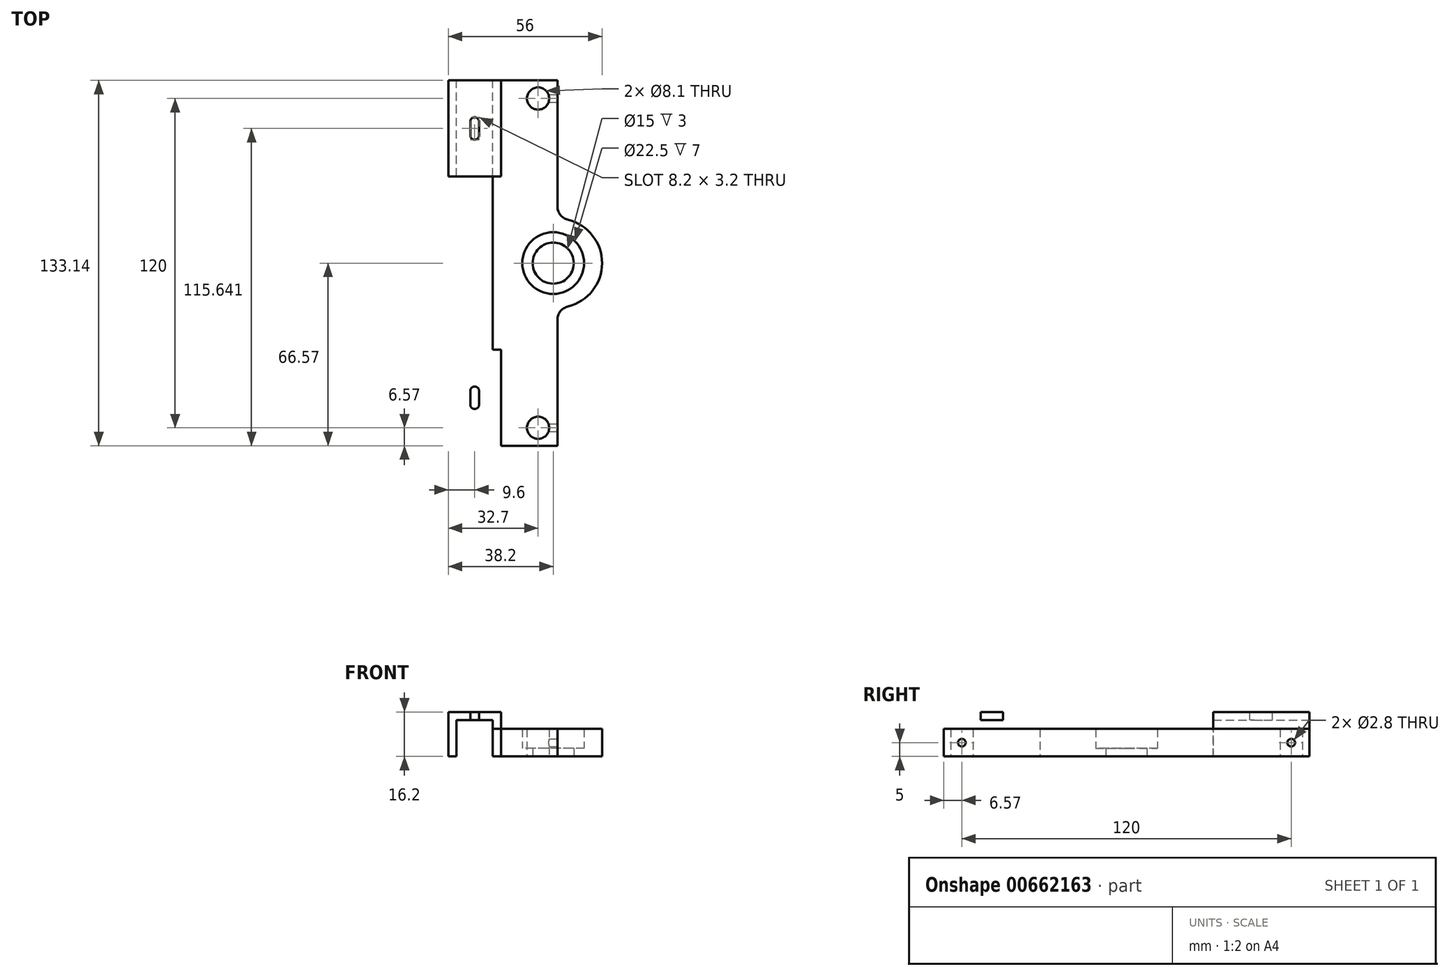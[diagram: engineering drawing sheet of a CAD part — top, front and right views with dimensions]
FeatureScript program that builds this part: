
annotation { "Feature Type Name" : "Feature", "Feature Type Description" : "" }
export const myFeature = defineFeature(function(context is Context, id is Id, definition is map)
    precondition{}
    {
        {
            var Q0;
            Q0=qCreatedBy(makeId("Top.planeOp"),FACE);
            var sketch = newSketch(context, id + "F0", { "sketchPlane" : qUnion([Q0])});
            skCircle(sketch, "E0", {"center": v(0, 0) * mm, "radius": 7.5 * mm});
            skLineSegment(sketch, "E1.rect.bottom", {"start": v(-22, -66.57) * mm, "end": v(22, -66.57) * mm});
            skLineSegment(sketch, "E1.rect.top", {"start": v(-22, 66.57) * mm, "end": v(22, 66.57) * mm});
            skLineSegment(sketch, "E1.rect.left", {"start": v(-22, -66.57) * mm, "end": v(-22, 66.57) * mm});
            skLineSegment(sketch, "E1.rect.right", {"start": v(22, -66.57) * mm, "end": v(22, 66.57) * mm});
            skCircle(sketch, "E2", {"center": v(0, 0) * mm, "radius": 11.25 * mm});
            skCircle(sketch, "E3", {"center": v(-5.5, -60) * mm, "radius": 4.05 * mm});
            skCircle(sketch, "E4", {"center": v(-5.5, 60) * mm, "radius": 4.05 * mm});
            skSolve(sketch);
        }
        {
            var Q0;
            Q0=makeQuery(id+"F0.imprint","IMPRINT",FACE,{"disambiguationData":[TD([[makeQuery(id+"F0.imprint","IMPRINT",EDGE,{"derivedFrom":sQuery(id+"F0.wireOp",EDGE,"E0")}),-1.0]])]});
            extrude(context, id + "F1", {"entities" : qUnion([Q0]), "depth" : 3 * mm});
        }
        {
            var Q0;
            Q0=makeQuery(id+"F0.imprint","IMPRINT",FACE,{"disambiguationData":[TD([[makeQuery(id+"F0.imprint","IMPRINT",EDGE,{"derivedFrom":sQuery(id+"F0.wireOp",EDGE,"E1.rect.bottom")}),1.0]])]});
            extrude(context, id + "F2", {"entities" : qUnion([Q0]), "operationType" : NewBodyOperationType.ADD, "depth" : 10 * mm});
        }
        {
            var Q0;
            Q0=makeQuery(id+"F2.opExtrude","CAP_FACE",FACE,{"disambiguationData":[OSD([sQuery(id+"F0.wireOp",EDGE,"E1.rect.bottom"),sQuery(id+"F0.wireOp",EDGE,"E1.rect.top"),sQuery(id+"F0.wireOp",EDGE,"E1.rect.left"),sQuery(id+"F0.wireOp",EDGE,"E1.rect.right"),sQuery(id+"F0.wireOp",EDGE,"E2"),sQuery(id+"F0.wireOp",EDGE,"E3"),sQuery(id+"F0.wireOp",EDGE,"E4")])],"isStart":false});
            var sketch = newSketch(context, id + "F3", { "sketchPlane" : qUnion([Q0])});
            skLineSegment(sketch, "E5", {"start": v(1.55, -66.57) * mm, "end": v(1.55, -16.25) * mm});
            skLineSegment(sketch, "E6", {"start": v(1.55, -16.25) * mm, "end": v(22, -16.25) * mm});
            skLineSegment(sketch, "E7", {"start": v(1.55, 66.57) * mm, "end": v(1.55, 16.25) * mm});
            skLineSegment(sketch, "E8", {"start": v(1.55, 16.25) * mm, "end": v(22, 16.25) * mm});
            skSolve(sketch);
        }
        {
            var Q0;
            {var subQ4=sQuery(id+"F3.wireOp",EDGE,"E5");Q0=makeQuery(id+"F3.imprint","IMPRINT",FACE,{"disambiguationData":[TD([[makeQuery(id+"F3.imprint","IMPRINT",EDGE,{"derivedFrom":subQ4}),-1.0]])]});}
            var Q1;
            {var subQ4=sQuery(id+"F3.wireOp",EDGE,"E7");Q1=makeQuery(id+"F3.imprint","IMPRINT",FACE,{"disambiguationData":[TD([[makeQuery(id+"F3.imprint","IMPRINT",EDGE,{"derivedFrom":subQ4}),1.0]])]});}
            extrude(context, id + "F4", {"entities" : qUnion([Q0, Q1]), "operationType" : NewBodyOperationType.REMOVE, "endBound" : BoundingType.UP_TO_NEXT, "oppositeDirection" : true, "depth" : 25 * mm});
        }
        {
            var Q0;
            Q0=makeQuery(id+"F2.opExtrude","CAP_FACE",FACE,{"disambiguationData":[OSD([sQuery(id+"F0.wireOp",EDGE,"E1.rect.bottom"),sQuery(id+"F0.wireOp",EDGE,"E1.rect.top"),sQuery(id+"F0.wireOp",EDGE,"E1.rect.left"),sQuery(id+"F0.wireOp",EDGE,"E1.rect.right"),sQuery(id+"F0.wireOp",EDGE,"E2"),sQuery(id+"F0.wireOp",EDGE,"E3"),sQuery(id+"F0.wireOp",EDGE,"E4")])],"isStart":false});
            var sketch = newSketch(context, id + "F5", { "sketchPlane" : qUnion([Q0])});
            skArc(sketch, "E9", {"start": v(1.55, -16.25) * mm, "mid": v(17.8, 0) * mm, "end": v(1.55, 16.25) * mm});
            skSolve(sketch);
        }
        {
            var Q0;
            Q0=makeQuery(id+"F5.imprint","IMPRINT",FACE,{"disambiguationData":[TD([[makeQuery(id+"F5.imprint","IMPRINT",EDGE,{"derivedFrom":sQuery(id+"F5.wireOp",EDGE,"E9")}),-1.0]])]});
            extrude(context, id + "F6", {"entities" : qUnion([Q0]), "operationType" : NewBodyOperationType.REMOVE, "endBound" : BoundingType.UP_TO_NEXT, "oppositeDirection" : true, "depth" : 25 * mm});
        }
        {
            var Q0;
            Q0=makeQuery(id+"F2.opExtrude","SWEPT_FACE",FACE,{"disambiguationData":[OSD([sQuery(id+"F0.wireOp",EDGE,"E1.rect.bottom")])]});
            var sketch = newSketch(context, id + "F7", { "sketchPlane" : qUnion([Q0])});
            skLineSegment(sketch, "E10", {"start": v(-22, 0) * mm, "end": v(-22, 0) * mm});
            skLineSegment(sketch, "E11", {"start": v(-22, 13.2) * mm, "end": v(-22, 0) * mm});
            skLineSegment(sketch, "E12", {"start": v(-22, 13.2) * mm, "end": v(-35.2, 13.2) * mm});
            skLineSegment(sketch, "E13", {"start": v(-35.2, 0) * mm, "end": v(-35.2, 13.2) * mm});
            skLineSegment(sketch, "E14", {"start": v(-35.2, 0) * mm, "end": v(-38.2, 0) * mm});
            skLineSegment(sketch, "E15", {"start": v(-38.2, 0) * mm, "end": v(-38.2, 16.2) * mm});
            skLineSegment(sketch, "E16", {"start": v(-22, 10) * mm, "end": v(-19, 10) * mm});
            skLineSegment(sketch, "E17", {"start": v(-19, 10) * mm, "end": v(-19, 16.2) * mm});
            skLineSegment(sketch, "E18", {"start": v(-19, 16.2) * mm, "end": v(-38.2, 16.2) * mm});
            skSolve(sketch);
        }
        {
            var Q0;
            Q0=qSketchRegion(id+"F7",true);
            var Q1;
            Q1=makeQuery(id+"F7.imprint","IMPRINT",FACE,{"disambiguationData":[TD([[makeQuery(id+"F7.imprint","IMPRINT",EDGE,{"derivedFrom":sQuery(id+"F7.wireOp",EDGE,"E10")}),-1.0]])]});
            var Q2;
            Q2=makeQuery(id+"F2.opExtrude","SWEPT_FACE",FACE,{"disambiguationData":[OSD([sQuery(id+"F0.wireOp",EDGE,"E1.rect.top")])]});
            extrude(context, id + "F8", {"entities" : qUnion([Q0, Q1]), "operationType" : NewBodyOperationType.ADD, "oppositeDirection" : true, "endBoundEntityFace" : qUnion([Q2]), "depth" : 35 * mm});
        }
        {
            var Q0;
            Q0=makeQuery(id+"F4.boolean.opBoolean","COPY",FACE,{"derivedFrom":makeQuery(id+"F4.opExtrude","SWEPT_FACE",FACE,{"disambiguationData":[OSD([sQuery(id+"F3.wireOp",EDGE,"E5")])]})});
            var sketch = newSketch(context, id + "F9", { "sketchPlane" : qUnion([Q0])});
            skCircle(sketch, "E19", {"center": v(-60, 5) * mm, "radius": 1.4 * mm});
            skPoint(sketch, "E19.centerSnap0", {"position": v(-66.57, 5) * mm});
            skCircle(sketch, "E20", {"center": v(60, 5) * mm, "radius": 1.4 * mm});
            skSolve(sketch);
        }
        {
            var Q0;
            Q0=makeQuery(id+"F9.imprint","IMPRINT",FACE,{"disambiguationData":[TD([[makeQuery(id+"F9.imprint","IMPRINT",EDGE,{"derivedFrom":sQuery(id+"F9.wireOp",EDGE,"E19")}),1.0]])]});
            var Q1;
            Q1=makeQuery(id+"F9.imprint","IMPRINT",FACE,{"disambiguationData":[TD([[makeQuery(id+"F9.imprint","IMPRINT",EDGE,{"derivedFrom":sQuery(id+"F9.wireOp",EDGE,"E20")}),1.0]])]});
            var Q2;
            Q2=makeQuery(id+"F1.opExtrude","SWEPT_BODY",BODY,{"disambiguationData":[OSD([sQuery(id+"F0.wireOp",EDGE,"E0"),sQuery(id+"F0.wireOp",EDGE,"E2")])]});
            extrude(context, id + "F10", {"entities" : qUnion([Q0, Q1]), "operationType" : NewBodyOperationType.REMOVE, "endBound" : BoundingType.UP_TO_BODY, "oppositeDirection" : true, "endBoundEntityBody" : qUnion([Q2]), "depth" : 25 * mm});
        }
        {
            var Q0;
            Q0=makeQuery(id+"F4.boolean.opBoolean","COPY",EDGE,{"derivedFrom":makeQuery(id+"F4.opExtrude","SWEPT_EDGE",EDGE,{"disambiguationData":[OSD([sQuery(id+"F0.wireOp",EDGE,"E1.rect.top"),sQuery(id+"F3.wireOp",EDGE,"E7")])]})});
            var Q1;
            Q1=makeQuery(id+"F4.boolean.opBoolean","COPY",EDGE,{"derivedFrom":makeQuery(id+"F4.opExtrude","SWEPT_EDGE",EDGE,{"disambiguationData":[OSD([sQuery(id+"F0.wireOp",EDGE,"E1.rect.bottom"),sQuery(id+"F3.wireOp",EDGE,"E5")])]})});
            var Q2;
            {var subQ0=sQuery(id+"F3.wireOp",EDGE,"E5");var subQ1=sQuery(id+"F3.wireOp",EDGE,"E6");Q2=makeQuery(id+"F6.boolean.opBoolean","MERGE",EDGE,{"derivedFrom":[makeQuery(id+"F4.boolean.opBoolean","COPY",EDGE,{"derivedFrom":makeQuery(id+"F4.opExtrude","SWEPT_EDGE",EDGE,{"disambiguationData":[OSD([subQ0,subQ1])]})}),makeQuery(id+"F6.opExtrude","SWEPT_EDGE",EDGE,{"disambiguationData":[OSD([subQ0,subQ1,sQuery(id+"F5.wireOp",EDGE,"E9")])]})]});}
            var Q3;
            {var subQ0=sQuery(id+"F3.wireOp",EDGE,"E7");var subQ1=sQuery(id+"F3.wireOp",EDGE,"E8");Q3=makeQuery(id+"F6.boolean.opBoolean","MERGE",EDGE,{"derivedFrom":[makeQuery(id+"F4.boolean.opBoolean","COPY",EDGE,{"derivedFrom":makeQuery(id+"F4.opExtrude","SWEPT_EDGE",EDGE,{"disambiguationData":[OSD([subQ0,subQ1])]})}),makeQuery(id+"F6.opExtrude","SWEPT_EDGE",EDGE,{"disambiguationData":[OSD([sQuery(id+"F0.wireOp",EDGE,"E0"),sQuery(id+"F0.wireOp",EDGE,"E1.rect.bottom"),sQuery(id+"F0.wireOp",EDGE,"E1.rect.top"),sQuery(id+"F0.wireOp",EDGE,"E1.rect.left"),sQuery(id+"F0.wireOp",EDGE,"E1.rect.right"),sQuery(id+"F0.wireOp",EDGE,"E2"),sQuery(id+"F0.wireOp",EDGE,"E3"),sQuery(id+"F0.wireOp",EDGE,"E4"),subQ0,subQ1])]})]});}
            fillet(context, id + "F11", {"entities" : qUnion([Q0, Q1, Q2, Q3]), "radius" : 5 * mm, "tangentPropagation" : true, "allowEdgeOverflow" : false});
        }
        {
            var Q0;
            Q0=makeQuery(id+"F2.opExtrude","SWEPT_FACE",FACE,{"disambiguationData":[OSD([sQuery(id+"F0.wireOp",EDGE,"E1.rect.top")])]});
            var sketch = newSketch(context, id + "F12", { "sketchPlane" : qUnion([Q0])});
            skLineSegment(sketch, "E21.0.3", {"start": v(19, 10) * mm, "end": v(19, 16.2) * mm});
            skLineSegment(sketch, "E21.0.4", {"start": v(19, 16.2) * mm, "end": v(38.2, 16.2) * mm});
            skLineSegment(sketch, "E21.0.5", {"start": v(38.2, 16.2) * mm, "end": v(38.2, 0) * mm});
            skLineSegment(sketch, "E21.0.6", {"start": v(38.2, 0) * mm, "end": v(35.2, 0) * mm});
            skLineSegment(sketch, "E21.0.7", {"start": v(35.2, 0) * mm, "end": v(35.2, 13.2) * mm});
            skLineSegment(sketch, "E21.0.8", {"start": v(35.2, 13.2) * mm, "end": v(22, 13.2) * mm});
            skLineSegment(sketch, "E22", {"start": v(19, 10) * mm, "end": v(22, 10) * mm});
            skLineSegment(sketch, "E23", {"start": v(22, 10) * mm, "end": v(22, 13.2) * mm});
            skSolve(sketch);
        }
        {
            var Q0;
            Q0=qSketchRegion(id+"F12",true);
            var Q1;
            {var subQ1=sQuery(id+"F12.wireOp",EDGE,"E21.0.3");Q1=makeQuery(id+"F12.imprint","IMPRINT",FACE,{"disambiguationData":[TD([[makeQuery(id+"F12.imprint","IMPRINT",EDGE,{"derivedFrom":subQ1}),-1.0]])]});}
            extrude(context, id + "F13", {"entities" : qUnion([Q0, Q1]), "operationType" : NewBodyOperationType.ADD, "oppositeDirection" : true, "depth" : 35 * mm});
        }
        {
            var Q0;
            Q0=makeQuery(id+"F8.opExtrude","SWEPT_FACE",FACE,{"disambiguationData":[OSD([sQuery(id+"F7.wireOp",EDGE,"E18")])]});
            var sketch = newSketch(context, id + "F14", { "sketchPlane" : qUnion([Q0])});
            skArc(sketch, "E24.0.startCap", {"start": v(-30.2, -46.57) * mm, "mid": v(-28.6, -44.97) * mm, "end": v(-27, -46.57) * mm});
            skArc(sketch, "E24.0.endCap", {"start": v(-27, -51.57) * mm, "mid": v(-28.6, -53.17) * mm, "end": v(-30.2, -51.57) * mm});
            skLineSegment(sketch, "E24.0.left", {"start": v(-27, -46.57) * mm, "end": v(-27, -51.57) * mm});
            skLineSegment(sketch, "E24.0.right", {"start": v(-30.2, -46.57) * mm, "end": v(-30.2, -51.57) * mm});
            skArc(sketch, "E25.MirrorCS", {"start": v(-30.2, 46.57) * mm, "mid": v(-28.6, 44.97) * mm, "end": v(-27, 46.57) * mm});
            skLineSegment(sketch, "E26.MirrorCS", {"start": v(-27, 46.57) * mm, "end": v(-27, 51.57) * mm});
            skLineSegment(sketch, "E27.MirrorCS", {"start": v(-30.2, 46.57) * mm, "end": v(-30.2, 51.57) * mm});
            skArc(sketch, "E28.MirrorCS", {"start": v(-27, 51.57) * mm, "mid": v(-28.6, 53.17) * mm, "end": v(-30.2, 51.57) * mm});
            skSolve(sketch);
        }
        {
            var Q0;
            Q0=makeQuery(id+"F14.imprint","IMPRINT",FACE,{"disambiguationData":[TD([[makeQuery(id+"F14.imprint","IMPRINT",EDGE,{"derivedFrom":sQuery(id+"F14.wireOp",EDGE,"E24.0.startCap")}),-1.0]])]});
            var Q1;
            Q1=makeQuery(id+"F14.imprint","IMPRINT",FACE,{"disambiguationData":[TD([[makeQuery(id+"F14.imprint","IMPRINT",EDGE,{"derivedFrom":sQuery(id+"F14.wireOp",EDGE,"E25.MirrorCS")}),1.0]])]});
            extrude(context, id + "F15", {"entities" : qUnion([Q0, Q1]), "operationType" : NewBodyOperationType.REMOVE, "oppositeDirection" : true, "depth" : 25 * mm});
        }
    });
